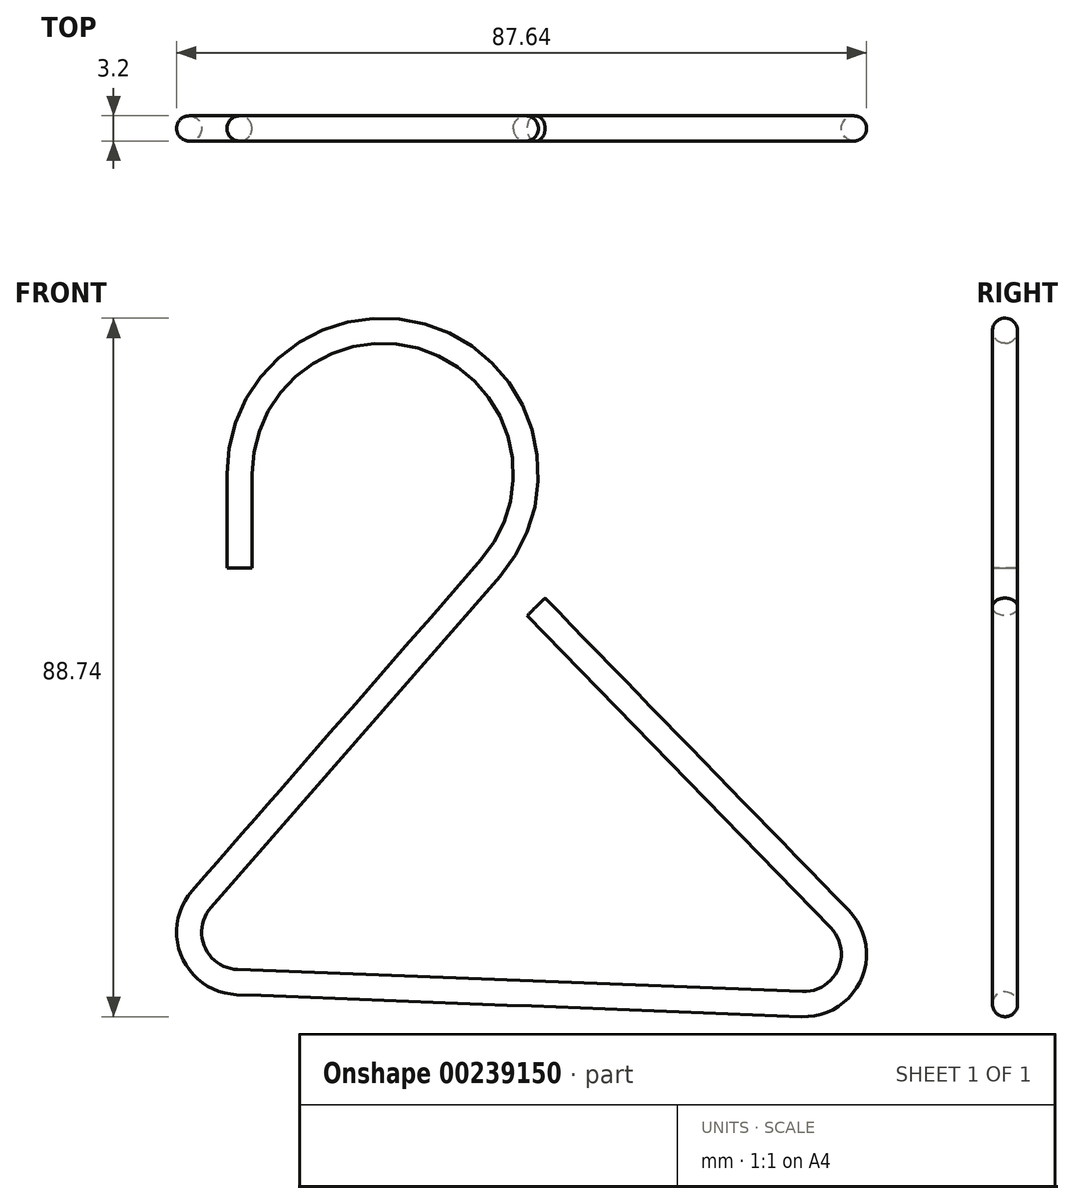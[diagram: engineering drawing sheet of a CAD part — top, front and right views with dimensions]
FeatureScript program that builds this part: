
annotation { "Feature Type Name" : "Feature", "Feature Type Description" : "" }
export const myFeature = defineFeature(function(context is Context, id is Id, definition is map)
    precondition{}
    {
        {
            var Q0;
            Q0=qCreatedBy(makeId("Front.planeOp"),FACE);
            var sketch = newSketch(context, id + "F0", { "sketchPlane" : qUnion([Q0])});
            skLineSegment(sketch, "E0", {"start": v(24.93, 0) * mm, "end": v(-11.79, -42.09) * mm});
            skLineSegment(sketch, "E1", {"start": v(-7.25, -52.6) * mm, "end": v(64.5, -55.4) * mm});
            skLineSegment(sketch, "E2", {"start": v(69.3, -44.63) * mm, "end": v(30.71, -4.94) * mm});
            skPoint(sketch, "E3.visualSharp", {"position": v(-20.52, -52.09) * mm});
            skArc(sketch, "E3.filletArc", {"start": v(-11.79, -42.09) * mm, "mid": v(-12.84, -48.78) * mm, "end": v(-7.25, -52.6) * mm});
            skPoint(sketch, "E4.visualSharp", {"position": v(80.37, -56.02) * mm});
            skArc(sketch, "E4.filletArc", {"start": v(64.5, -55.4) * mm, "mid": v(70.55, -51.64) * mm, "end": v(69.3, -44.63) * mm});
            skArc(sketch, "E5", {"start": v(24.93, 0) * mm, "mid": v(17.61, 28.98) * mm, "end": v(-6.96, 11.96) * mm});
            skLineSegment(sketch, "E6", {"start": v(-6.96, 11.96) * mm, "end": v(-6.96, 0) * mm});
            skSolve(sketch);
        }
        {
            var Q0;
            Q0=qCreatedBy(makeId("Top.planeOp"),FACE);
            var sketch = newSketch(context, id + "F1", { "sketchPlane" : qUnion([Q0])});
            skCircle(sketch, "E7", {"center": v(-6.96, 0) * mm, "radius": 1.6 * mm});
            skSolve(sketch);
        }
        {
            var Q0;
            Q0 = qSketchRegion(id + "F1", true);
            var Q1;
            Q1 = qConstructionFilter(qBodyType(qCreatedBy(id + "F0" ,EDGE), BodyType.WIRE), ConstructionObject.NO);
            sweep(context, id + "F2", {"profiles" : qUnion([Q0]), "path" : qUnion([Q1])});
        }
    });
